# Revit family: Sanitary_Installation-Systems_AXOR_01400CHN-AXOR-iBox-universal-2-Basic-set222
name_source: partatom
category: Plumbing Fixtures
revit_build: Autodesk Revit 2018 (Build: 20170223_1515(x64)
units: mm (PartAtom-declared; Revit-internal decimal feet)

## family parameters
Always vertical = No
Cut with Voids When Loaded = No
OmniClass Number = 23.31.11.19.11
OmniClass Title = Thermostatically Controlled Faucet Mixing Valves
Part Type = Normal
Room Calculation Point = No
Round Connector Dimension = Use Diameter
Shared = No
Work Plane-Based = Yes

## types (1)
- 01400CHN AXOR iBox universal 2 Basic set
    Always visible = Yes
    BIMobject category = Installation Systems
    Connector Description = Water Inlet 19.05 mm
    Default Elevation = 1219.2 mm  [stored 4 ft]
    Description = AXOR iBox universal 2 Basic set
    Design country = Germany
    Diameter = 19.05 mm
    EAN code = 4059625316917
    Edition number = 1
    IFC Classification = Valve
    Manufacturer = AXOR
    Manufacturer country = Germany
    Manufacturer name = AXOR
    Material 1 = AXOR - Plastic - Black
    Material 2 = AXOR - Plastic - Light Green
    Material 3 = AXOR - Plastic - Green
    Material 4 = AXOR - Metal - Brass
    Model = 01400CHN
    OmniClass Code = 23-31 11 19 11
    OmniClass Description = Thermostatically Controlled Faucet Mixing Valves
    Outlet Connector Description = Water Outlet 19.05 mm
    Outlet Diameter = 19.05 mm
    Product Guid = b6c37d3d-39d0-46c9-bdb4-3c1f4eadcdf2
    Product SKU = 01400CHN
    Product data url = https://bimobject.com
    Product family = AXOR iBox universal 2
    Product group = Concealed Basic set bath/shower mixers
    Product name = 01400CHN AXOR iBox universal 2 Basic set
    Product url = https://www.axor-design.com
    QR code = https://bimobject.com
    UNSPSC Code = 3018
    URL = https://www.axor-design.com
    Weight Net (Kg) = 1.7

note: [stored X ft] marks values corroborated as IEEE doubles in the binary element streams (Revit-internal decimal feet)

## geometry (parser evidence)
native form markers: Sweep x1
no freeform markers — native parametric forms only
